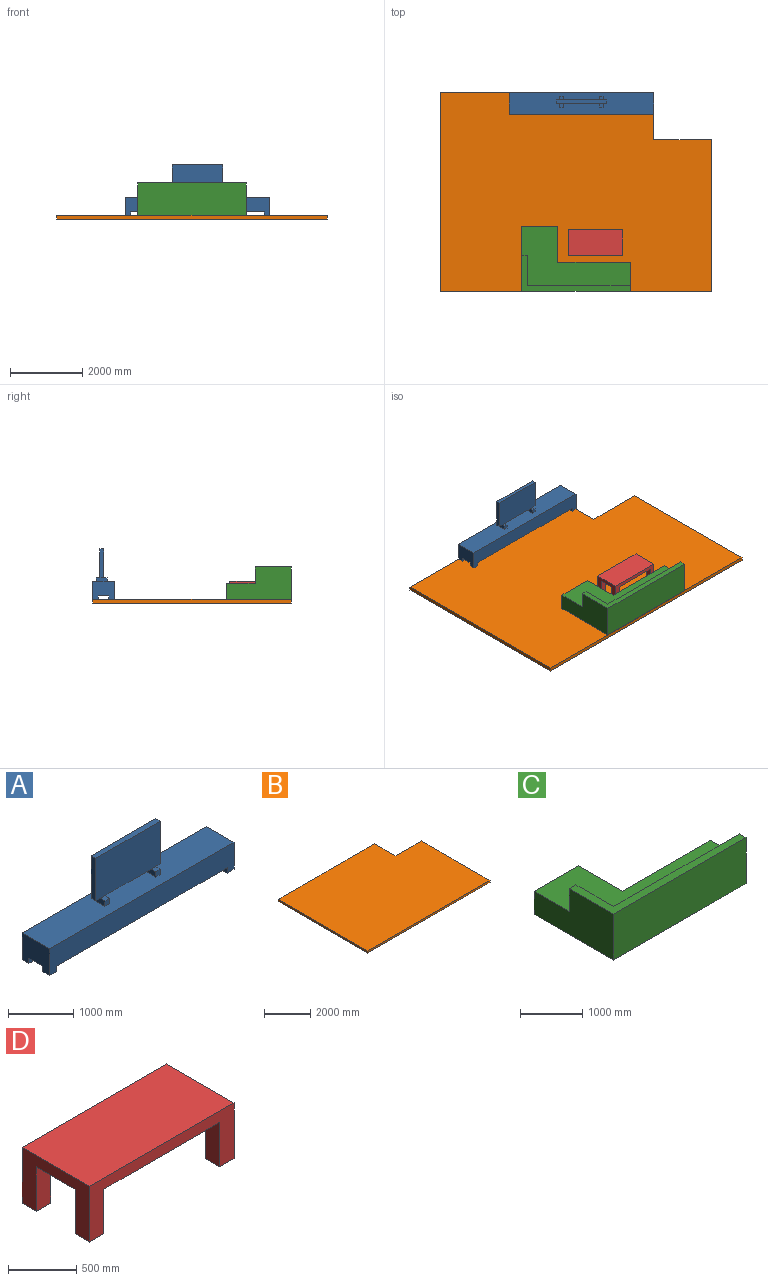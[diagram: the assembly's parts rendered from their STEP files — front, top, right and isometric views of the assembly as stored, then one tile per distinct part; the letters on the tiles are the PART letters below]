
ASSEMBLY  parts=4 mates=3
PART A: 38 faces, bbox 4000x600x1400 mm
  f0: plane 100x100mm, normal (0,0,1), area 10000mm2, adj f20,f21,f23,f32
  f1: plane 100x100mm, normal (0,0,1), area 10000mm2, adj f25,f26,f27,f32
  f2: plane 4000x600mm, normal (0,0,1), area 2340000mm2, adj f6,f7,f8,f9,f20,f21,f22,f23
  f3: plane 150x150mm, normal (0,0,-1), area 22500mm2, adj f6,f7,f11,f12
  f4: plane 150x150mm, normal (0,0,-1), area 22500mm2, adj f7,f9,f13,f14
  f5: plane 150x150mm, normal (0,0,-1), area 22500mm2, adj f8,f9,f15,f16
  f6: plane 4000x500mm, normal (0,-1,0), area 1630000mm2, adj f2,f3,f7,f8,f10,f11,f18,f19
  f7: plane 600x500mm, normal (-1,0,0), area 270000mm2, adj f2,f3,f4,f6,f9,f12,f13,f19
  f8: plane 600x500mm, normal (1,0,0), area 270000mm2, adj f2,f5,f6,f9,f10,f16,f17,f19
  f9: plane 4000x500mm, normal (0,1,0), area 1630000mm2, adj f2,f4,f5,f7,f8,f14,f15,f19
  f10: plane 150x150mm, normal (0,0,-1), area 22500mm2, adj f6,f8,f17,f18
  f11: plane 150x100mm, normal (1,0,0), area 15000mm2, adj f3,f6,f12,f19
  f12: plane 150x100mm, normal (0,1,0), area 15000mm2, adj f3,f7,f11,f19
  f13: plane 150x100mm, normal (0,-1,0), area 15000mm2, adj f4,f7,f14,f19
  f14: plane 150x100mm, normal (1,0,0), area 15000mm2, adj f4,f9,f13,f19
  f15: plane 150x100mm, normal (-1,0,0), area 15000mm2, adj f5,f9,f16,f19
  f16: plane 150x100mm, normal (0,-1,0), area 15000mm2, adj f5,f8,f15,f19
  f17: plane 150x100mm, normal (0,1,0), area 15000mm2, adj f8,f10,f18,f19
  f18: plane 150x100mm, normal (-1,0,0), area 15000mm2, adj f6,f10,f17,f19
  f19: plane 4000x600mm, normal (0,0,-1), area 2310000mm2, adj f6,f7,f8,f9,f11,f12,f13,f14
  f20: plane 100x100mm, normal (0,1,0), area 10000mm2, adj f0,f2,f21,f23
  f21: plane 300x100mm, normal (-1,0,0), area 30000mm2, adj f0,f2,f20,f22,f24,f30
  f22: plane 100x100mm, normal (0,-1,0), area 10000mm2, adj f2,f21,f23,f24
  f23: plane 300x100mm, normal (1,0,0), area 30000mm2, adj f0,f2,f20,f22,f24,f31
  f24: plane 100x100mm, normal (0,0,1), area 10000mm2, adj f21,f22,f23,f34
  f25: plane 300x100mm, normal (1,0,0), area 30000mm2, adj f1,f2,f26,f28,f29,f37
  f26: plane 100x100mm, normal (0,1,0), area 10000mm2, adj f1,f2,f25,f27
  f27: plane 300x100mm, normal (-1,0,0), area 30000mm2, adj f1,f2,f26,f28,f29,f31
  f28: plane 100x100mm, normal (0,-1,0), area 10000mm2, adj f2,f25,f27,f29
  f29: plane 100x100mm, normal (0,0,1), area 10000mm2, adj f25,f27,f28,f34
  f30: plane 100x100mm, normal (0,0,-1), area 10000mm2, adj f21,f32,f33,f34
  f31: plane 1000x100mm, normal (0,0,-1), area 100000mm2, adj f23,f27,f32,f34
  f32: plane 1400x800mm, normal (0,1,0), area 1120000mm2, adj f0,f1,f30,f31,f33,f35,f36,f37
  f33: plane 800x100mm, normal (-1,0,0), area 80000mm2, adj f30,f32,f34,f36
  f34: plane 1400x800mm, normal (0,-1,0), area 1120000mm2, adj f24,f29,f30,f31,f33,f35,f36,f37
  f35: plane 800x100mm, normal (1,0,0), area 80000mm2, adj f32,f34,f36,f37
  f36: plane 1400x100mm, normal (0,0,1), area 140000mm2, adj f32,f33,f34,f35
  f37: plane 100x100mm, normal (0,0,-1), area 10000mm2, adj f25,f32,f34,f35
PART B: 8 faces, bbox 7500x5500x100 mm
  f0: plane 5500x100mm, normal (-1,0,0), area 550000mm2, adj f1,f5,f6,f7
  f1: plane 7500x100mm, normal (0,-1,0), area 750000mm2, adj f0,f2,f6,f7
  f2: plane 4200x100mm, normal (1,0,0), area 420000mm2, adj f1,f3,f6,f7
  f3: plane 1600x100mm, normal (0,1,0), area 160000mm2, adj f2,f4,f6,f7
  f4: plane 1300x100mm, normal (1,0,0), area 130000mm2, adj f3,f5,f6,f7
  f5: plane 5900x100mm, normal (0,1,0), area 590000mm2, adj f0,f4,f6,f7
  f6: plane 7500x5500mm, normal (0,0,1), area 39170000mm2, adj f0,f1,f2,f3,f4,f5
  f7: plane 7500x5500mm, normal (0,0,-1), area 39170000mm2, adj f0,f1,f2,f3,f4,f5
PART C: 12 faces, bbox 3000x1800x900 mm
  f0: plane 900x800mm, normal (1,0,0), area 427500mm2, adj f3,f5,f6,f7,f10,f11
  f1: plane 1000x450mm, normal (0,1,0), area 450000mm2, adj f2,f4,f7,f11
  f2: plane 1800x900mm, normal (-1,0,0), area 1260000mm2, adj f1,f5,f6,f7,f8,f11
  f3: plane 2000x450mm, normal (0,1,0), area 900000mm2, adj f0,f4,f7,f11
  f4: plane 1000x450mm, normal (1,0,0), area 450000mm2, adj f1,f3,f7,f11
  f5: plane 3000x900mm, normal (0,-1,0), area 2700000mm2, adj f0,f2,f6,f7
  f6: plane 3000x1000mm, normal (0,0,1), area 577500mm2, adj f0,f2,f5,f8,f9,f10
  f7: plane 3000x1800mm, normal (0,0,-1), area 3400000mm2, adj f0,f1,f2,f3,f4,f5
  f8: plane 450x150mm, normal (0,1,0), area 67500mm2, adj f2,f6,f9,f11
  f9: plane 850x450mm, normal (1,0,0), area 382500mm2, adj f6,f8,f10,f11
  f10: plane 2850x450mm, normal (0,1,0), area 1282500mm2, adj f0,f6,f9,f11
  f11: plane 3000x1650mm, normal (0,0,1), area 2822500mm2, adj f0,f1,f2,f3,f4,f8,f9,f10
PART D: 18 faces, bbox 1500x700x500 mm
  f0: plane 150x150mm, normal (0,0,-1), area 22500mm2, adj f5,f6,f9,f10
  f1: plane 150x150mm, normal (0,0,-1), area 22500mm2, adj f3,f5,f11,f12
  f2: plane 150x150mm, normal (0,0,-1), area 22500mm2, adj f3,f4,f13,f14
  f3: plane 1500x500mm, normal (0,1,0), area 270000mm2, adj f1,f2,f4,f5,f7,f12,f13,f17
  f4: plane 700x500mm, normal (1,0,0), area 190000mm2, adj f2,f3,f6,f7,f8,f14,f15,f17
  f5: plane 700x500mm, normal (-1,0,0), area 190000mm2, adj f0,f1,f3,f6,f7,f10,f11,f17
  f6: plane 1500x500mm, normal (0,-1,0), area 270000mm2, adj f0,f4,f5,f7,f8,f9,f16,f17
  f7: plane 1500x700mm, normal (0,0,1), area 1050000mm2, adj f3,f4,f5,f6
  f8: plane 150x150mm, normal (0,0,-1), area 22500mm2, adj f4,f6,f15,f16
  f9: plane 400x150mm, normal (1,0,0), area 60000mm2, adj f0,f6,f10,f17
  f10: plane 400x150mm, normal (0,1,0), area 60000mm2, adj f0,f5,f9,f17
  f11: plane 400x150mm, normal (0,-1,0), area 60000mm2, adj f1,f5,f12,f17
  f12: plane 400x150mm, normal (1,0,0), area 60000mm2, adj f1,f3,f11,f17
  f13: plane 400x150mm, normal (-1,0,0), area 60000mm2, adj f2,f3,f14,f17
  f14: plane 400x150mm, normal (0,-1,0), area 60000mm2, adj f2,f4,f13,f17
  f15: plane 400x150mm, normal (0,1,0), area 60000mm2, adj f4,f8,f16,f17
  f16: plane 400x150mm, normal (-1,0,0), area 60000mm2, adj f6,f8,f15,f17
  f17: plane 1500x700mm, normal (0,0,-1), area 960000mm2, adj f3,f4,f5,f6,f9,f10,f11,f12
PLACE A t=(6404.09,4900,100)mm
PLACE B at identity fixed
PLACE C t=(2250,0,100)mm
PLACE D t=(2150.71,-262.49,100)mm
MATE fastened C.f5 <-> B.f1  axis (0,-1,0) through (3750,0,100)mm
MATE fastened D.f8 <-> C.f7  axis (0,0,-1) through (5050,1000,100)mm
MATE fastened A.f5 <-> B.f6  axis (0,0,-1) through (5900,5500,100)mm
